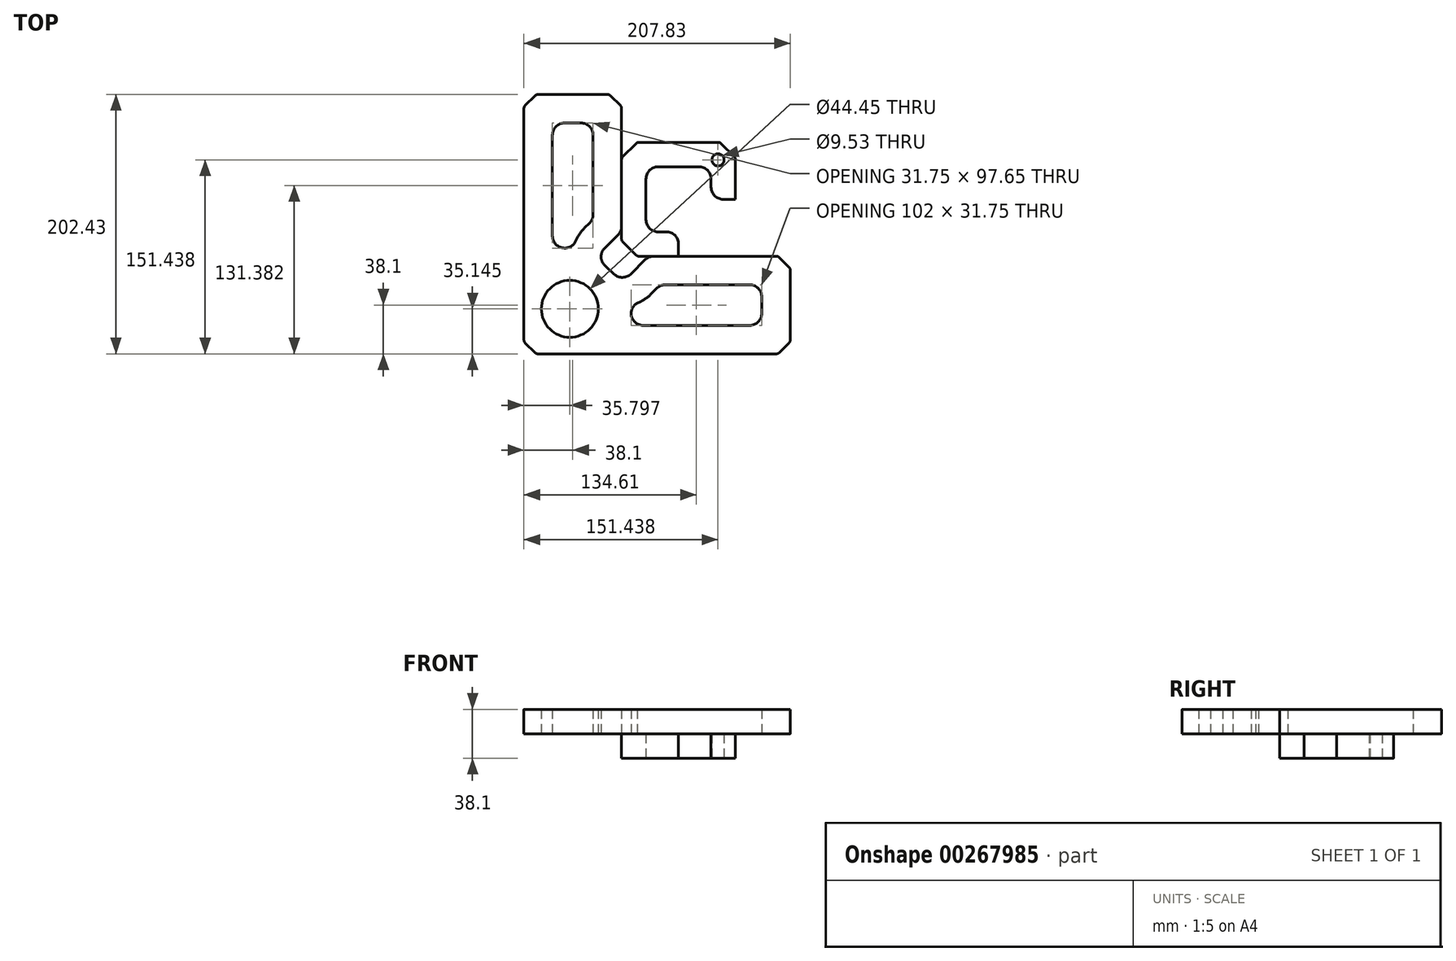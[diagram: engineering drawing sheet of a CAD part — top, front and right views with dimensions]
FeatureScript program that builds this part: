
annotation { "Feature Type Name" : "Feature", "Feature Type Description" : "" }
export const myFeature = defineFeature(function(context is Context, id is Id, definition is map)
    precondition{}
    {
        {
            var Q0;
            Q0=qCreatedBy(makeId("Top.planeOp"),FACE);
            var sketch = newSketch(context, id + "F0", { "sketchPlane" : qUnion([Q0])});
            skLineSegment(sketch, "E0.bottom", {"start": v(-30.98, -44.45) * mm, "end": v(0, -44.45) * mm});
            skLineSegment(sketch, "E0.left", {"start": v(-44.45, -30.98) * mm, "end": v(-44.45, 0) * mm});
            skPoint(sketch, "E0.middle", {"position": v(0, 0) * mm});
            skPoint(sketch, "E1.visualSharp", {"position": v(-44.45, -44.45) * mm});
            skLineSegment(sketch, "E2", {"start": v(-43.52, -33.22) * mm, "end": v(-33.22, -43.52) * mm});
            skPoint(sketch, "E3.visualSharp", {"position": v(-44.45, -32.3) * mm});
            skArc(sketch, "E3.filletArc", {"start": v(-44.45, -30.98) * mm, "mid": v(-44.2, -32.2) * mm, "end": v(-43.52, -33.22) * mm});
            skPoint(sketch, "E4.visualSharp", {"position": v(-32.3, -44.45) * mm});
            skArc(sketch, "E4.filletArc", {"start": v(-33.22, -43.52) * mm, "mid": v(-32.2, -44.2) * mm, "end": v(-30.98, -44.45) * mm});
            skLineSegment(sketch, "E5.0", {"start": v(-25.4, -25.4) * mm, "end": v(0, -25.4) * mm});
            skLineSegment(sketch, "E5.1", {"start": v(-25.4, -25.4) * mm, "end": v(-25.4, 0) * mm});
            skLineSegment(sketch, "E6", {"start": v(-25.4, 0) * mm, "end": v(-44.45, 0) * mm});
            skPoint(sketch, "E6.endSnap0", {"position": v(-25.4, 0) * mm});
            skLineSegment(sketch, "E7", {"start": v(0, -25.4) * mm, "end": v(0, -44.45) * mm});
            skArc(sketch, "E8.MirrorCS", {"start": v(-44.45, 30.98) * mm, "mid": v(-44.2, 32.2) * mm, "end": v(-43.52, 33.22) * mm});
            skArc(sketch, "E9.MirrorCS", {"start": v(-33.22, 43.52) * mm, "mid": v(-32.2, 44.2) * mm, "end": v(-30.98, 44.45) * mm});
            skPoint(sketch, "E10.MirrorP", {"position": v(-44.45, 44.45) * mm});
            skLineSegment(sketch, "E11.MirrorCS", {"start": v(-43.52, 33.22) * mm, "end": v(-33.22, 43.52) * mm});
            skLineSegment(sketch, "E12.MirrorCS", {"start": v(-30.98, 44.45) * mm, "end": v(0, 44.45) * mm});
            skLineSegment(sketch, "E13.MirrorCS", {"start": v(-44.45, 30.98) * mm, "end": v(-44.45, 0) * mm});
            skLineSegment(sketch, "E14.MirrorCS", {"start": v(0, 25.4) * mm, "end": v(0, 44.45) * mm});
            skPoint(sketch, "E15.MirrorP", {"position": v(-44.45, 32.3) * mm});
            skLineSegment(sketch, "E16.MirrorCS", {"start": v(-25.4, 25.4) * mm, "end": v(0, 25.4) * mm});
            skLineSegment(sketch, "E17.MirrorCS", {"start": v(-25.4, 25.4) * mm, "end": v(-25.4, 0) * mm});
            skPoint(sketch, "E18.MirrorP", {"position": v(-32.3, 44.45) * mm});
            skArc(sketch, "E19.MirrorCS", {"start": v(33.22, -43.52) * mm, "mid": v(32.2, -44.2) * mm, "end": v(30.98, -44.45) * mm});
            skArc(sketch, "E20.MirrorCS", {"start": v(33.22, 43.52) * mm, "mid": v(32.2, 44.2) * mm, "end": v(30.98, 44.45) * mm});
            skArc(sketch, "E21.MirrorCS", {"start": v(44.45, -30.98) * mm, "mid": v(44.2, -32.2) * mm, "end": v(43.52, -33.22) * mm});
            skArc(sketch, "E22.MirrorCS", {"start": v(44.45, 30.98) * mm, "mid": v(44.2, 32.2) * mm, "end": v(43.52, 33.22) * mm});
            skLineSegment(sketch, "E23.MirrorCS", {"start": v(43.52, -33.22) * mm, "end": v(33.22, -43.52) * mm});
            skPoint(sketch, "E24.MirrorP", {"position": v(25.4, 0) * mm});
            skPoint(sketch, "E25.MirrorP", {"position": v(44.45, -44.45) * mm});
            skPoint(sketch, "E26.MirrorP", {"position": v(44.45, 44.45) * mm});
            skPoint(sketch, "E27.MirrorP", {"position": v(44.45, 32.3) * mm});
            skLineSegment(sketch, "E28.MirrorCS", {"start": v(30.98, -44.45) * mm, "end": v(0, -44.45) * mm});
            skLineSegment(sketch, "E29.MirrorCS", {"start": v(44.45, 30.98) * mm, "end": v(44.45, 0) * mm});
            skLineSegment(sketch, "E30.MirrorCS", {"start": v(25.4, 25.4) * mm, "end": v(0, 25.4) * mm});
            skLineSegment(sketch, "E31.MirrorCS", {"start": v(43.52, 33.22) * mm, "end": v(33.22, 43.52) * mm});
            skPoint(sketch, "E32.MirrorP", {"position": v(32.3, -44.45) * mm});
            skLineSegment(sketch, "E33.MirrorCS", {"start": v(30.98, 44.45) * mm, "end": v(0, 44.45) * mm});
            skLineSegment(sketch, "E34.MirrorCS", {"start": v(25.4, -25.4) * mm, "end": v(25.4, 0) * mm});
            skPoint(sketch, "E35.MirrorP", {"position": v(44.45, -32.3) * mm});
            skPoint(sketch, "E36.MirrorP", {"position": v(32.3, 44.45) * mm});
            skLineSegment(sketch, "E37.MirrorCS", {"start": v(25.4, -25.4) * mm, "end": v(0, -25.4) * mm});
            skLineSegment(sketch, "E38.MirrorCS", {"start": v(44.45, -30.98) * mm, "end": v(44.45, 0) * mm});
            skLineSegment(sketch, "E39.MirrorCS", {"start": v(25.4, 25.4) * mm, "end": v(25.4, 0) * mm});
            skLineSegment(sketch, "E40.MirrorCS", {"start": v(25.4, 0) * mm, "end": v(44.45, 0) * mm});
            skLineSegment(sketch, "E41", {"start": v(25.4, 25.4) * mm, "end": v(38.37, 38.37) * mm, "construction": true});
            skLineSegment(sketch, "E42", {"start": v(25.4, 25.4) * mm, "end": v(30.79, 30.79) * mm, "construction": true});
            skCircle(sketch, "E43", {"center": v(30.79, 30.79) * mm, "radius": 4.76 * mm});
            skSolve(sketch);
        }
        {
            var Q0;
            Q0=makeQuery(id+"F0.imprint","IMPRINT",FACE,{"disambiguationData":[TD([[makeQuery(id+"F0.imprint","IMPRINT",EDGE,{"derivedFrom":sQuery(id+"F0.wireOp",EDGE,"E0.bottom")}),1.0]])]});
            var Q1;
            Q1=makeQuery(id+"F0.imprint","IMPRINT",FACE,{"disambiguationData":[TD([[makeQuery(id+"F0.imprint","IMPRINT",EDGE,{"derivedFrom":sQuery(id+"F0.wireOp",EDGE,"E6")}),-1.0]])]});
            var Q2;
            Q2=makeQuery(id+"F0.imprint","IMPRINT",FACE,{"disambiguationData":[TD([[makeQuery(id+"F0.imprint","IMPRINT",EDGE,{"derivedFrom":sQuery(id+"F0.wireOp",EDGE,"E14.MirrorCS")}),-1.0]])]});
            var Q3;
            Q3=makeQuery(id+"F0.imprint","IMPRINT",FACE,{"disambiguationData":[TD([[makeQuery(id+"F0.imprint","IMPRINT",EDGE,{"derivedFrom":sQuery(id+"F0.wireOp",EDGE,"E19.MirrorCS")}),-1.0]])]});
            extrude(context, id + "F1", {"entities" : qUnion([Q0, Q1, Q2, Q3]), "depth" : 19.05 * mm});
        }
        {
            var Q0;
            Q0=makeQuery(id+"F1.opExtrude","SWEPT_EDGE",EDGE,{"disambiguationData":[OSD([sQuery(id+"F0.wireOp",EDGE,"E16.MirrorCS"),sQuery(id+"F0.wireOp",EDGE,"E17.MirrorCS")])]});
            var Q1;
            Q1=makeQuery(id+"F1.opExtrude","SWEPT_EDGE",EDGE,{"disambiguationData":[OSD([sQuery(id+"F0.wireOp",EDGE,"E30.MirrorCS"),sQuery(id+"F0.wireOp",EDGE,"E39.MirrorCS")])]});
            var Q2;
            Q2=makeQuery(id+"F1.opExtrude","SWEPT_EDGE",EDGE,{"disambiguationData":[OSD([sQuery(id+"F0.wireOp",EDGE,"E34.MirrorCS"),sQuery(id+"F0.wireOp",EDGE,"E37.MirrorCS")])]});
            var Q3;
            Q3=makeQuery(id+"F1.opExtrude","SWEPT_EDGE",EDGE,{"disambiguationData":[OSD([sQuery(id+"F0.wireOp",EDGE,"E5.0"),sQuery(id+"F0.wireOp",EDGE,"E5.1")])]});
            fillet(context, id + "F2", {"entities" : qUnion([Q0, Q1, Q2, Q3]), "radius" : 9.52 * mm, "tangentPropagation" : true, "allowEdgeOverflow" : false});
        }
        {
            var Q0;
            Q0=makeQuery(id+"F1.opExtrude","CAP_FACE",FACE,{"disambiguationData":[OSD([sQuery(id+"F0.wireOp",EDGE,"E0.bottom"),sQuery(id+"F0.wireOp",EDGE,"E0.left"),sQuery(id+"F0.wireOp",EDGE,"E2"),sQuery(id+"F0.wireOp",EDGE,"E3.filletArc"),sQuery(id+"F0.wireOp",EDGE,"E4.filletArc"),sQuery(id+"F0.wireOp",EDGE,"E5.0"),sQuery(id+"F0.wireOp",EDGE,"E5.1"),sQuery(id+"F0.wireOp",EDGE,"E8.MirrorCS"),sQuery(id+"F0.wireOp",EDGE,"E9.MirrorCS"),sQuery(id+"F0.wireOp",EDGE,"E11.MirrorCS"),sQuery(id+"F0.wireOp",EDGE,"E12.MirrorCS"),sQuery(id+"F0.wireOp",EDGE,"E13.MirrorCS"),sQuery(id+"F0.wireOp",EDGE,"E16.MirrorCS"),sQuery(id+"F0.wireOp",EDGE,"E17.MirrorCS"),sQuery(id+"F0.wireOp",EDGE,"E19.MirrorCS"),sQuery(id+"F0.wireOp",EDGE,"E20.MirrorCS"),sQuery(id+"F0.wireOp",EDGE,"E21.MirrorCS"),sQuery(id+"F0.wireOp",EDGE,"E22.MirrorCS"),sQuery(id+"F0.wireOp",EDGE,"E23.MirrorCS"),sQuery(id+"F0.wireOp",EDGE,"E28.MirrorCS"),sQuery(id+"F0.wireOp",EDGE,"E29.MirrorCS"),sQuery(id+"F0.wireOp",EDGE,"E30.MirrorCS"),sQuery(id+"F0.wireOp",EDGE,"E31.MirrorCS"),sQuery(id+"F0.wireOp",EDGE,"E33.MirrorCS"),sQuery(id+"F0.wireOp",EDGE,"E34.MirrorCS"),sQuery(id+"F0.wireOp",EDGE,"E37.MirrorCS"),sQuery(id+"F0.wireOp",EDGE,"E38.MirrorCS"),sQuery(id+"F0.wireOp",EDGE,"E39.MirrorCS"),sQuery(id+"F0.wireOp",EDGE,"E43")])],"isStart":false});
            var sketch = newSketch(context, id + "F3", { "sketchPlane" : qUnion([Q0])});
            skLineSegment(sketch, "E44", {"start": v(-44.45, 30.98) * mm, "end": v(-44.45, -20.94) * mm});
            skLineSegment(sketch, "E45", {"start": v(21.45, -44.45) * mm, "end": v(-19.37, -44.45) * mm});
            skLineSegment(sketch, "E46.0", {"start": v(30.98, -120.65) * mm, "end": v(-111.12, -120.65) * mm});
            skLineSegment(sketch, "E46.1", {"start": v(-120.65, 30.98) * mm, "end": v(-120.65, -111.12) * mm});
            skLineSegment(sketch, "E47", {"start": v(-26.1, -47.24) * mm, "end": v(-37.04, -58.18) * mm});
            skLineSegment(sketch, "E48", {"start": v(-47.24, -27.68) * mm, "end": v(-57.66, -38.1) * mm});
            skLineSegment(sketch, "E49", {"start": v(-57.4, -51.82) * mm, "end": v(-50.25, -58.43) * mm});
            skArc(sketch, "E50.filletArc", {"start": v(-57.66, -38.1) * mm, "mid": v(-60.44, -45.01) * mm, "end": v(-57.4, -51.82) * mm});
            skPoint(sketch, "E51.visualSharp", {"position": v(-43.52, -64.66) * mm});
            skArc(sketch, "E51.filletArc", {"start": v(-50.25, -58.43) * mm, "mid": v(-43.6, -60.96) * mm, "end": v(-37.04, -58.18) * mm});
            skPoint(sketch, "E52.visualSharp", {"position": v(-23.31, -44.45) * mm});
            skArc(sketch, "E52.filletArc", {"start": v(-19.37, -44.45) * mm, "mid": v(-23.01, -45.18) * mm, "end": v(-26.1, -47.24) * mm});
            skPoint(sketch, "E53.visualSharp", {"position": v(-44.45, -24.89) * mm});
            skArc(sketch, "E53.filletArc", {"start": v(-47.24, -27.68) * mm, "mid": v(-45.18, -24.59) * mm, "end": v(-44.45, -20.94) * mm});
            skPoint(sketch, "E54.visualSharp", {"position": v(30.98, -44.45) * mm});
            skLineSegment(sketch, "E55", {"start": v(21.45, -44.45) * mm, "end": v(30.98, -44.45) * mm});
            skLineSegment(sketch, "E56.0", {"start": v(-53.98, 81.78) * mm, "end": v(-111.12, 81.78) * mm});
            skLineSegment(sketch, "E57", {"start": v(30.98, -44.45) * mm, "end": v(77.66, -44.45) * mm});
            skLineSegment(sketch, "E58", {"start": v(77.66, -120.65) * mm, "end": v(30.98, -120.65) * mm});
            skLineSegment(sketch, "E59", {"start": v(-44.45, 30.98) * mm, "end": v(-44.45, 72.25) * mm});
            skLineSegment(sketch, "E60", {"start": v(-120.65, 72.25) * mm, "end": v(-120.65, 30.98) * mm});
            skLineSegment(sketch, "E61.0", {"start": v(-98.43, 50.03) * mm, "end": v(-98.43, 30.98) * mm});
            skLineSegment(sketch, "E61.1", {"start": v(-76.2, 59.55) * mm, "end": v(-88.9, 59.55) * mm});
            skLineSegment(sketch, "E61.2", {"start": v(-66.67, 30.98) * mm, "end": v(-66.67, 50.03) * mm});
            skLineSegment(sketch, "E61.3", {"start": v(-66.67, 30.98) * mm, "end": v(-66.67, -11.73) * mm});
            skLineSegment(sketch, "E61.4", {"start": v(-69.46, -18.47) * mm, "end": v(-73.37, -22.38) * mm});
            skLineSegment(sketch, "E61.5", {"start": v(30.98, -66.67) * mm, "end": v(55.43, -66.68) * mm});
            skLineSegment(sketch, "E61.6", {"start": v(64.96, -76.2) * mm, "end": v(64.96, -88.9) * mm});
            skLineSegment(sketch, "E61.7", {"start": v(55.43, -98.43) * mm, "end": v(30.98, -98.42) * mm});
            skLineSegment(sketch, "E61.8", {"start": v(30.98, -98.43) * mm, "end": v(-27.51, -98.43) * mm});
            skLineSegment(sketch, "E61.9", {"start": v(21.45, -66.67) * mm, "end": v(30.98, -66.67) * mm});
            skLineSegment(sketch, "E61.10", {"start": v(21.45, -66.67) * mm, "end": v(-10.16, -66.67) * mm});
            skLineSegment(sketch, "E61.11", {"start": v(-16.9, -69.46) * mm, "end": v(-21.32, -73.9) * mm});
            skLineSegment(sketch, "E61.14", {"start": v(-98.43, 30.98) * mm, "end": v(-98.43, -28.57) * mm});
            skArc(sketch, "E61.15", {"start": v(-73.37, -22.38) * mm, "mid": v(-77.21, -27.03) * mm, "end": v(-80.1, -32.32) * mm});
            skPoint(sketch, "E62.visualSharp", {"position": v(-120.65, 81.78) * mm});
            skPoint(sketch, "E63.visualSharp", {"position": v(-44.45, 81.78) * mm});
            skPoint(sketch, "E64.visualSharp", {"position": v(-66.67, 59.55) * mm});
            skArc(sketch, "E64.filletArc", {"start": v(-66.67, 50.03) * mm, "mid": v(-69.46, 56.76) * mm, "end": v(-76.2, 59.55) * mm});
            skPoint(sketch, "E65.visualSharp", {"position": v(-98.43, 59.55) * mm});
            skArc(sketch, "E65.filletArc", {"start": v(-88.9, 59.55) * mm, "mid": v(-95.64, 56.76) * mm, "end": v(-98.43, 50.03) * mm});
            skPoint(sketch, "E66.visualSharp", {"position": v(64.96, -66.68) * mm});
            skArc(sketch, "E66.filletArc", {"start": v(64.96, -76.2) * mm, "mid": v(62.17, -69.46) * mm, "end": v(55.43, -66.68) * mm});
            skPoint(sketch, "E67.visualSharp", {"position": v(64.96, -98.43) * mm});
            skArc(sketch, "E67.filletArc", {"start": v(55.43, -98.43) * mm, "mid": v(62.17, -95.64) * mm, "end": v(64.96, -88.9) * mm});
            skPoint(sketch, "E68.visualSharp", {"position": v(-120.65, -120.65) * mm});
            skLineSegment(sketch, "E69", {"start": v(87.18, -53.98) * mm, "end": v(87.18, -111.13) * mm});
            skPoint(sketch, "E70.visualSharp", {"position": v(87.18, -44.45) * mm});
            skPoint(sketch, "E71.visualSharp", {"position": v(87.18, -120.65) * mm});
            skPoint(sketch, "E72.visualSharp", {"position": v(-14.1, -66.67) * mm});
            skArc(sketch, "E72.filletArc", {"start": v(-10.16, -66.67) * mm, "mid": v(-13.8, -67.4) * mm, "end": v(-16.9, -69.46) * mm});
            skPoint(sketch, "E73.visualSharp", {"position": v(-66.67, -15.68) * mm});
            skArc(sketch, "E73.filletArc", {"start": v(-69.46, -18.47) * mm, "mid": v(-67.4, -15.38) * mm, "end": v(-66.67, -11.73) * mm});
            skLineSegment(sketch, "E74", {"start": v(-88.86, -38.1) * mm, "end": v(-88.9, -38.1) * mm});
            skArc(sketch, "E75.trimOffspring", {"start": v(-32.21, -81.01) * mm, "mid": v(-26.4, -78.01) * mm, "end": v(-21.32, -73.9) * mm});
            skArc(sketch, "E76.trimOffspring", {"start": v(-82.58, -47.23) * mm, "mid": v(-82.58, -47.23) * mm, "end": v(-82.58, -47.24) * mm});
            skPoint(sketch, "E77.visualSharp", {"position": v(-37.04, -98.43) * mm});
            skArc(sketch, "E77.filletArc", {"start": v(-37.04, -88.9) * mm, "mid": v(-34.25, -95.64) * mm, "end": v(-27.51, -98.43) * mm});
            skPoint(sketch, "E78.visualSharp", {"position": v(-98.43, -38.1) * mm});
            skArc(sketch, "E78.filletArc", {"start": v(-98.43, -28.57) * mm, "mid": v(-95.64, -35.3) * mm, "end": v(-88.9, -38.1) * mm});
            skPoint(sketch, "E79.visualSharp", {"position": v(-81.95, -38.1) * mm});
            skArc(sketch, "E79.filletArc", {"start": v(-88.86, -38.1) * mm, "mid": v(-83.61, -36.52) * mm, "end": v(-80.1, -32.32) * mm});
            skPoint(sketch, "E80.orphan", {"position": v(-82.67, -44.83) * mm});
            skArc(sketch, "E81", {"start": v(-32.21, -81.01) * mm, "mid": v(-35.65, -84.33) * mm, "end": v(-37.04, -88.9) * mm});
            skLineSegment(sketch, "E82", {"start": v(-120.65, 72.25) * mm, "end": v(-111.12, 81.78) * mm});
            skLineSegment(sketch, "E83", {"start": v(-53.98, 81.78) * mm, "end": v(-44.45, 72.25) * mm});
            skLineSegment(sketch, "E84", {"start": v(-120.65, -111.12) * mm, "end": v(-111.12, -120.65) * mm});
            skLineSegment(sketch, "E85", {"start": v(77.66, -120.65) * mm, "end": v(87.18, -111.13) * mm});
            skLineSegment(sketch, "E86", {"start": v(87.18, -53.98) * mm, "end": v(77.66, -44.45) * mm});
            skLineSegment(sketch, "E87", {"start": v(-115.89, -115.89) * mm, "end": v(-53.82, -55.12) * mm, "construction": true});
            skCircle(sketch, "E88", {"center": v(-84.85, -85.5) * mm, "radius": 22.23 * mm});
            skSolve(sketch);
        }
        {
            var Q0;
            Q0=makeQuery(id+"F3.imprint","IMPRINT",FACE,{"disambiguationData":[TD([[makeQuery(id+"F3.imprint","IMPRINT",EDGE,{"derivedFrom":sQuery(id+"F3.wireOp",EDGE,"E44")}),1.0]])]});
            extrude(context, id + "F4", {"entities" : qUnion([Q0]), "depth" : 19.05 * mm});
        }
        {
            var Q0;
            Q0=makeQuery(id+"F4.opExtrude","SWEPT_EDGE",EDGE,{"disambiguationData":[OSD([sQuery(id+"F3.wireOp",EDGE,"E56.0"),sQuery(id+"F3.wireOp",EDGE,"E82")])]});
            var Q1;
            Q1=makeQuery(id+"F4.opExtrude","SWEPT_EDGE",EDGE,{"disambiguationData":[OSD([sQuery(id+"F3.wireOp",EDGE,"E56.0"),sQuery(id+"F3.wireOp",EDGE,"E83")])]});
            var Q2;
            Q2=makeQuery(id+"F4.opExtrude","SWEPT_EDGE",EDGE,{"disambiguationData":[OSD([sQuery(id+"F3.wireOp",EDGE,"E59"),sQuery(id+"F3.wireOp",EDGE,"E83")])]});
            var Q3;
            Q3=makeQuery(id+"F4.opExtrude","SWEPT_EDGE",EDGE,{"disambiguationData":[OSD([sQuery(id+"F3.wireOp",EDGE,"E57"),sQuery(id+"F3.wireOp",EDGE,"E86")])]});
            var Q4;
            Q4=makeQuery(id+"F4.opExtrude","SWEPT_EDGE",EDGE,{"disambiguationData":[OSD([sQuery(id+"F3.wireOp",EDGE,"E69"),sQuery(id+"F3.wireOp",EDGE,"E86")])]});
            var Q5;
            Q5=makeQuery(id+"F4.opExtrude","SWEPT_EDGE",EDGE,{"disambiguationData":[OSD([sQuery(id+"F3.wireOp",EDGE,"E69"),sQuery(id+"F3.wireOp",EDGE,"E85")])]});
            var Q6;
            Q6=makeQuery(id+"F4.opExtrude","SWEPT_EDGE",EDGE,{"disambiguationData":[OSD([sQuery(id+"F3.wireOp",EDGE,"E58"),sQuery(id+"F3.wireOp",EDGE,"E85")])]});
            var Q7;
            Q7=makeQuery(id+"F4.opExtrude","SWEPT_EDGE",EDGE,{"disambiguationData":[OSD([sQuery(id+"F3.wireOp",EDGE,"E60"),sQuery(id+"F3.wireOp",EDGE,"E82")])]});
            var Q8;
            Q8=makeQuery(id+"F4.opExtrude","SWEPT_EDGE",EDGE,{"disambiguationData":[OSD([sQuery(id+"F3.wireOp",EDGE,"E46.1"),sQuery(id+"F3.wireOp",EDGE,"E84")])]});
            var Q9;
            Q9=makeQuery(id+"F4.opExtrude","SWEPT_EDGE",EDGE,{"disambiguationData":[OSD([sQuery(id+"F3.wireOp",EDGE,"E46.0"),sQuery(id+"F3.wireOp",EDGE,"E84")])]});
            fillet(context, id + "F5", {"entities" : qUnion([Q0, Q1, Q2, Q3, Q4, Q5, Q6, Q7, Q8, Q9]), "radius" : 3.17 * mm, "tangentPropagation" : true, "allowEdgeOverflow" : false});
        }
    });
